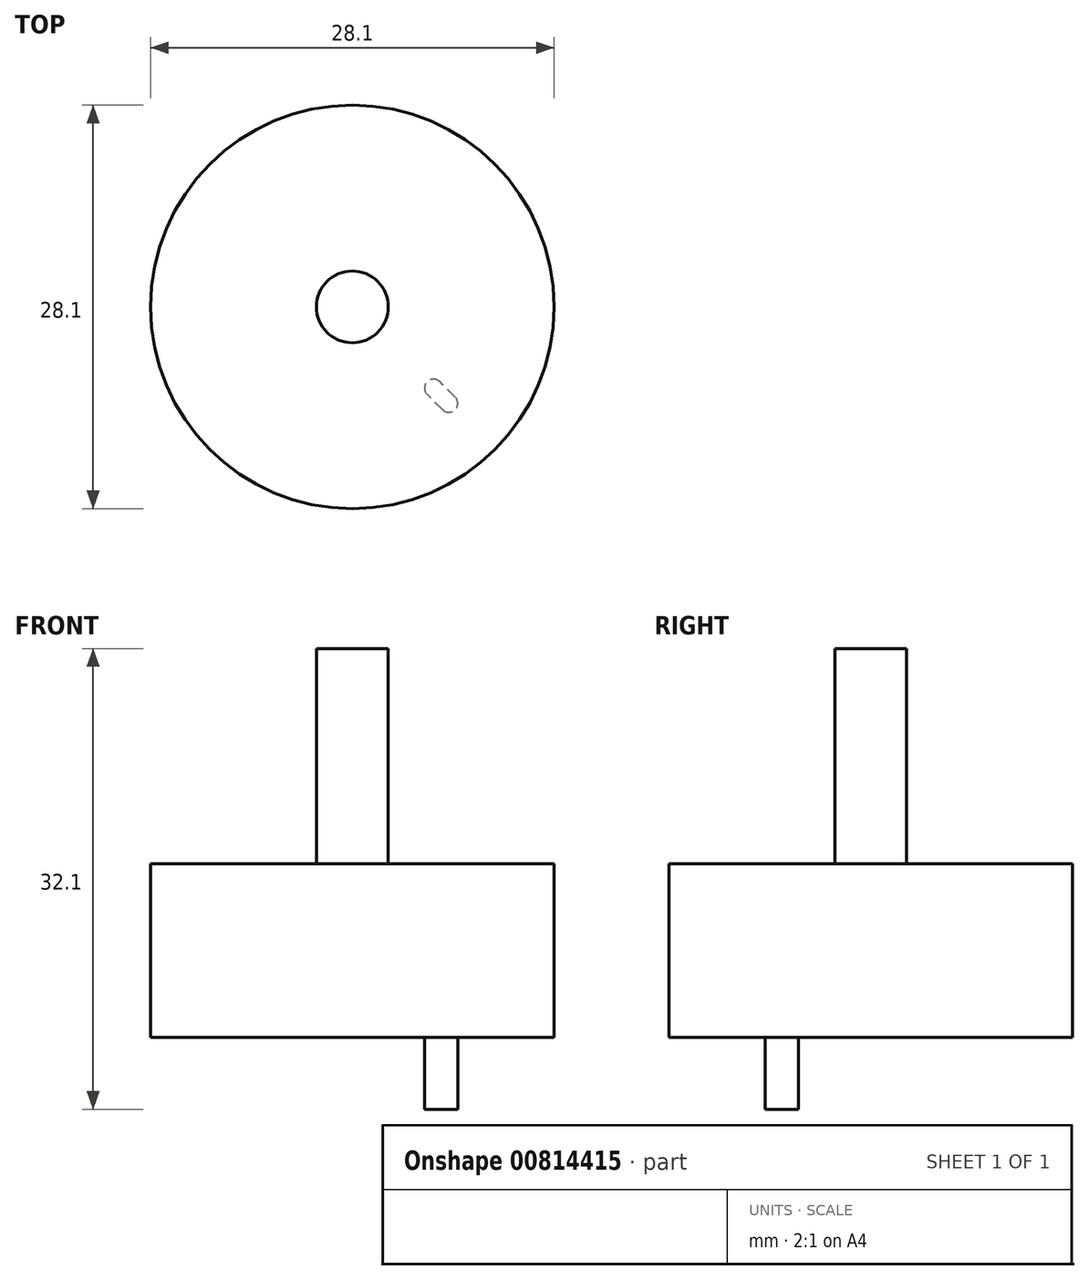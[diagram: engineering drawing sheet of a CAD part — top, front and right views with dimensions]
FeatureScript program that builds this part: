
annotation { "Feature Type Name" : "Feature", "Feature Type Description" : "" }
export const myFeature = defineFeature(function(context is Context, id is Id, definition is map)
    precondition{}
    {
        {
            var Q0;
            Q0=qCreatedBy(makeId("Top.planeOp"),FACE);
            var sketch = newSketch(context, id + "F0", { "sketchPlane" : qUnion([Q0])});
            skCircle(sketch, "E0", {"center": v(0, 0) * mm, "radius": 14.05 * mm});
            skSolve(sketch);
        }
        {
            var Q0;
            Q0=makeQuery(id+"F0.imprint","IMPRINT",FACE,{"disambiguationData":[TD([[makeQuery(id+"F0.imprint","IMPRINT",EDGE,{"derivedFrom":sQuery(id+"F0.wireOp",EDGE,"E0")}),1.0]])]});
            extrude(context, id + "F1", {"entities" : qUnion([Q0]), "depth" : 17.1 * mm, "offsetDistance" : 25.4 * mm});
        }
        {
            var Q0;
            Q0=makeQuery(id+"F1.opExtrude","CAP_FACE",FACE,{"disambiguationData":[OSD([sQuery(id+"F0.wireOp",EDGE,"E0")])],"isStart":false});
            var sketch = newSketch(context, id + "F2", { "sketchPlane" : qUnion([Q0])});
            skCircle(sketch, "E1", {"center": v(0, 0) * mm, "radius": 2.5 * mm});
            skSolve(sketch);
        }
        {
            var Q0;
            Q0=makeQuery(id+"F2.imprint","IMPRINT",FACE,{"disambiguationData":[TD([[makeQuery(id+"F2.imprint","IMPRINT",EDGE,{"derivedFrom":sQuery(id+"F2.wireOp",EDGE,"E1")}),1.0]])]});
            extrude(context, id + "F3", {"entities" : qUnion([Q0]), "operationType" : NewBodyOperationType.ADD, "depth" : 15 * mm, "offsetDistance" : 25.4 * mm});
        }
        {
            var Q0;
            Q0=makeQuery(id+"F1.opExtrude","CAP_FACE",FACE,{"disambiguationData":[OSD([sQuery(id+"F0.wireOp",EDGE,"E0")])],"isStart":true});
            var sketch = newSketch(context, id + "F4", { "sketchPlane" : qUnion([Q0])});
            skCircle(sketch, "E2", {"center": v(0, 0) * mm, "radius": 9.5 * mm, "construction": true});
            skLineSegment(sketch, "E3.bottom", {"start": v(6.72, -6.72) * mm, "end": v(-6.72, -6.72) * mm, "construction": true});
            skLineSegment(sketch, "E3.top", {"start": v(6.72, 6.72) * mm, "end": v(-6.72, 6.72) * mm, "construction": true});
            skLineSegment(sketch, "E3.left", {"start": v(6.72, -6.72) * mm, "end": v(6.72, 6.72) * mm, "construction": true});
            skLineSegment(sketch, "E3.right", {"start": v(-6.72, -6.72) * mm, "end": v(-6.72, 6.72) * mm, "construction": true});
            skCircle(sketch, "E4", {"center": v(0, 0) * mm, "radius": 8 * mm, "construction": true});
            skLineSegment(sketch, "E5.bottom", {"start": v(5.66, -5.66) * mm, "end": v(-5.66, -5.66) * mm, "construction": true});
            skLineSegment(sketch, "E5.top", {"start": v(5.66, 5.66) * mm, "end": v(-5.66, 5.66) * mm, "construction": true});
            skLineSegment(sketch, "E5.left", {"start": v(5.66, -5.66) * mm, "end": v(5.66, 5.66) * mm, "construction": true});
            skLineSegment(sketch, "E5.right", {"start": v(-5.66, -5.66) * mm, "end": v(-5.66, 5.66) * mm, "construction": true});
            skLineSegment(sketch, "E6", {"start": v(6.72, 6.72) * mm, "end": v(5.66, 5.66) * mm});
            skArc(sketch, "E7.0.startCap", {"start": v(6.28, 7.16) * mm, "mid": v(7.16, 7.16) * mm, "end": v(7.16, 6.28) * mm});
            skArc(sketch, "E7.0.endCap", {"start": v(6.1, 5.21) * mm, "mid": v(5.21, 5.21) * mm, "end": v(5.21, 6.1) * mm});
            skLineSegment(sketch, "E7.0.left", {"start": v(7.16, 6.28) * mm, "end": v(6.1, 5.21) * mm});
            skLineSegment(sketch, "E7.0.right", {"start": v(6.28, 7.16) * mm, "end": v(5.21, 6.1) * mm});
            skLineSegment(sketch, "E8.1.0", {"start": v(-7.16, 6.28) * mm, "end": v(-6.1, 5.21) * mm});
            skLineSegment(sketch, "E8.1.1", {"start": v(-6.28, 7.16) * mm, "end": v(-5.21, 6.1) * mm});
            skArc(sketch, "E8.1.2", {"start": v(-7.16, 6.28) * mm, "mid": v(-7.16, 7.16) * mm, "end": v(-6.28, 7.16) * mm});
            skArc(sketch, "E8.1.3", {"start": v(-5.21, 6.1) * mm, "mid": v(-5.21, 5.21) * mm, "end": v(-6.1, 5.21) * mm});
            skLineSegment(sketch, "E8.1.4", {"start": v(-6.72, 6.72) * mm, "end": v(-5.66, 5.66) * mm});
            skLineSegment(sketch, "E8.2.0", {"start": v(-6.28, -7.16) * mm, "end": v(-5.21, -6.1) * mm});
            skLineSegment(sketch, "E8.2.1", {"start": v(-7.16, -6.28) * mm, "end": v(-6.1, -5.21) * mm});
            skArc(sketch, "E8.2.2", {"start": v(-6.28, -7.16) * mm, "mid": v(-7.16, -7.16) * mm, "end": v(-7.16, -6.28) * mm});
            skArc(sketch, "E8.2.3", {"start": v(-6.1, -5.21) * mm, "mid": v(-5.21, -5.21) * mm, "end": v(-5.21, -6.1) * mm});
            skLineSegment(sketch, "E8.2.4", {"start": v(-6.72, -6.72) * mm, "end": v(-5.66, -5.66) * mm});
            skLineSegment(sketch, "E8.3.0", {"start": v(7.16, -6.28) * mm, "end": v(6.1, -5.21) * mm});
            skLineSegment(sketch, "E8.3.1", {"start": v(6.28, -7.16) * mm, "end": v(5.21, -6.1) * mm});
            skArc(sketch, "E8.3.2", {"start": v(7.16, -6.28) * mm, "mid": v(7.16, -7.16) * mm, "end": v(6.28, -7.16) * mm});
            skArc(sketch, "E8.3.3", {"start": v(5.21, -6.1) * mm, "mid": v(5.21, -5.21) * mm, "end": v(6.1, -5.21) * mm});
            skLineSegment(sketch, "E8.3.4", {"start": v(6.72, -6.72) * mm, "end": v(5.66, -5.66) * mm});
            skSolve(sketch);
        }
        {
            var Q0;
            Q0=makeQuery(id+"F4.imprint","IMPRINT",FACE,{"disambiguationData":[TD([[makeQuery(id+"F4.imprint","IMPRINT",EDGE,{"derivedFrom":sQuery(id+"F4.wireOp",EDGE,"E8.1.0")}),1.0]])]});
            var Q1;
            Q1=makeQuery(id+"F4.imprint","IMPRINT",FACE,{"disambiguationData":[TD([[makeQuery(id+"F4.imprint","IMPRINT",EDGE,{"derivedFrom":sQuery(id+"F4.wireOp",EDGE,"E7.0.startCap")}),-1.0]])]});
            var Q2;
            Q2=makeQuery(id+"F4.imprint","IMPRINT",FACE,{"disambiguationData":[TD([[makeQuery(id+"F4.imprint","IMPRINT",EDGE,{"derivedFrom":sQuery(id+"F4.wireOp",EDGE,"E8.3.0")}),1.0]])]});
            var Q3;
            Q3=makeQuery(id+"F4.imprint","IMPRINT",FACE,{"disambiguationData":[TD([[makeQuery(id+"F4.imprint","IMPRINT",EDGE,{"derivedFrom":sQuery(id+"F4.wireOp",EDGE,"E8.2.0")}),1.0]])]});
            var Q4;
            Q4=sQuery(id+"F4.wireOp",EDGE,"3E7uNhke-DrPj-qnbf-6Anz-Z0Zb7eQR0XeY");
            var Q5;
            Q5=sQuery(id+"F4.wireOp",EDGE,"xO4Em0Rv-9CIH-eCI5-yB2v-aXhoqpjQdeY8");
            var Q6;
            Q6=sQuery(id+"F4.wireOp",EDGE,"4cf7a38f-8d83-40b8-a645-45f6d76d8543.1.0");
            var Q7;
            Q7=sQuery(id+"F4.wireOp",EDGE,"7cea4d0c-d9ed-45aa-88e6-e636b83b7583.1.0");
            extrude(context, id + "F5", {"entities" : qUnion([Q0, Q1, Q2, Q3]), "operationType" : NewBodyOperationType.REMOVE, "surfaceEntities" : qUnion([Q4, Q5, Q6, Q7]), "oppositeDirection" : true, "depth" : 5 * mm, "offsetDistance" : 25.4 * mm});
        }
    });
